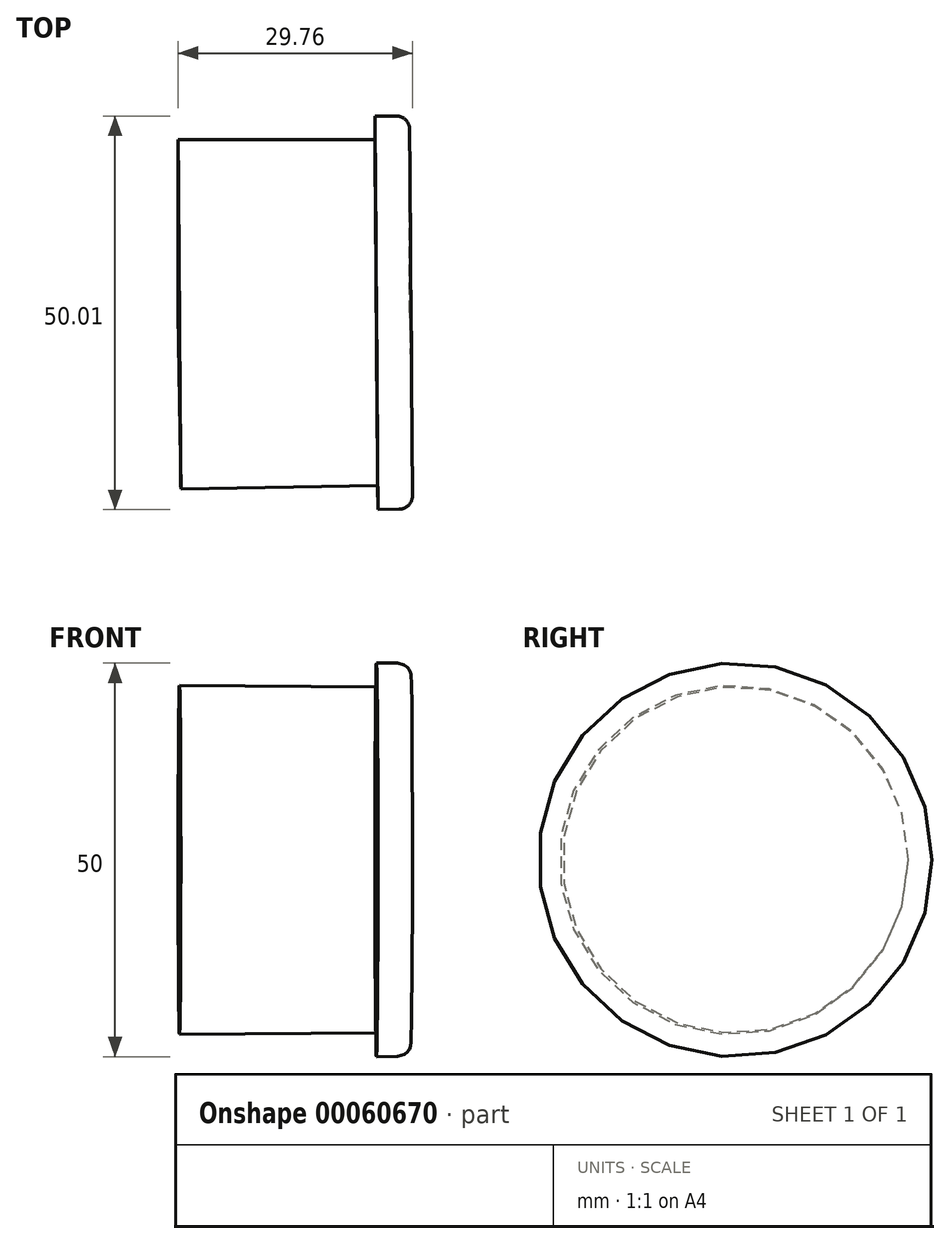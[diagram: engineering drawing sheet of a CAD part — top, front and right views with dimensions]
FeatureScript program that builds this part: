
annotation { "Feature Type Name" : "Feature", "Feature Type Description" : "" }
export const myFeature = defineFeature(function(context is Context, id is Id, definition is map)
    precondition{}
    {
        {
            var Q0;
            Q0=qCreatedBy(makeId("Top.planeOp"),FACE);
            var sketch = newSketch(context, id + "F0", { "sketchPlane" : qUnion([Q0])});
            skLineSegment(sketch, "E0", {"start": v(-38.82, 22.46) * mm, "end": v(-13.82, 22.46) * mm});
            skLineSegment(sketch, "E1", {"start": v(-38.82, 22.46) * mm, "end": v(-38.82, 0.29) * mm});
            skLineSegment(sketch, "E2", {"start": v(-13.82, 22.46) * mm, "end": v(-13.82, 25.48) * mm});
            skLineSegment(sketch, "E3", {"start": v(-13.82, 25.48) * mm, "end": v(-11.12, 25.48) * mm});
            skPoint(sketch, "E4.visualSharp", {"position": v(-7.48, 25.48) * mm});
            skArc(sketch, "E4.filletArc", {"start": v(-9.42, 23.78) * mm, "mid": v(-9.92, 24.98) * mm, "end": v(-11.12, 25.48) * mm});
            skLineSegment(sketch, "E5", {"start": v(-13.82, 0.29) * mm, "end": v(-13.82, 22.46) * mm});
            skLineSegment(sketch, "E6", {"start": v(-9.42, 23.78) * mm, "end": v(-9.42, 0.51) * mm});
            skLineSegment(sketch, "E7", {"start": v(-38.82, 0.29) * mm, "end": v(-13.82, 0.29) * mm, "construction": true});
            skLineSegment(sketch, "E8", {"start": v(-9.42, 0.51) * mm, "end": v(-38.82, 0.29) * mm});
            skSolve(sketch);
        }
        {
            var Q0;
            {var subQ1=sQuery(id+"F0.wireOp",EDGE,"E2");Q0=makeQuery(id+"F0.imprint","IMPRINT",FACE,{"disambiguationData":[TD([[makeQuery(id+"F0.imprint","IMPRINT",EDGE,{"derivedFrom":subQ1}),-1.0]])]});}
            var Q1;
            {var subQ0=sQuery(id+"F0.wireOp",EDGE,"E0");Q1=makeQuery(id+"F0.imprint","IMPRINT",FACE,{"disambiguationData":[TD([[makeQuery(id+"F0.imprint","IMPRINT",EDGE,{"derivedFrom":subQ0}),-1.0]])]});}
            var Q2;
            Q2=sQuery(id+"F0.wireOp",EDGE,"E8");
            revolve(context, id + "F1", {"entities" : qUnion([Q0, Q1]), "axis" : qUnion([Q2]), "revolveType" : RevolveType.FULL});
        }
        {
            var Q0;
            Q0=qCreatedBy(makeId("Right.planeOp"),FACE);
            cPlane(context, id + "F2", {"entities" : qUnion([Q0]), "cplaneType" : CPlaneType.OFFSET, "offset" : 50 * mm, "width" : 150 * mm, "height" : 150 * mm});
        }
        {
            var Q0;
            Q0=qCreatedBy(id+"F2.planeOp",FACE);
            var sketch = newSketch(context, id + "F3", { "sketchPlane" : qUnion([Q0])});
            skCircle(sketch, "E9.cCircle", {"center": v(0, 0) * mm, "radius": 7.75 * mm, "construction": true});
            skLineSegment(sketch, "E9.0", {"start": v(4.47, -7.75) * mm, "end": v(-4.47, -7.75) * mm});
            skLineSegment(sketch, "E9.1", {"start": v(-4.47, -7.75) * mm, "end": v(-8.95, 0) * mm});
            skLineSegment(sketch, "E9.2", {"start": v(-8.95, 0) * mm, "end": v(-4.47, 7.75) * mm});
            skLineSegment(sketch, "E9.3", {"start": v(-4.47, 7.75) * mm, "end": v(4.47, 7.75) * mm});
            skLineSegment(sketch, "E9.4", {"start": v(4.47, 7.75) * mm, "end": v(8.95, 0) * mm});
            skLineSegment(sketch, "E9.5", {"start": v(8.95, 0) * mm, "end": v(4.47, -7.75) * mm});
            skPoint(sketch, "E9.0.midPoint", {"position": v(0, -7.75) * mm});
            skSolve(sketch);
        }
        {
            var Q0;
            Q0=makeQuery(id+"F3.imprint","IMPRINT",FACE,{"disambiguationData":[TD([[makeQuery(id+"F3.imprint","IMPRINT",EDGE,{"derivedFrom":sQuery(id+"F3.wireOp",EDGE,"E9.0")}),-1.0]])]});
            extrude(context, id + "F4", {"entities" : qUnion([Q0]), "operationType" : NewBodyOperationType.REMOVE, "oppositeDirection" : true, "depth" : 15 * mm});
        }
    });
